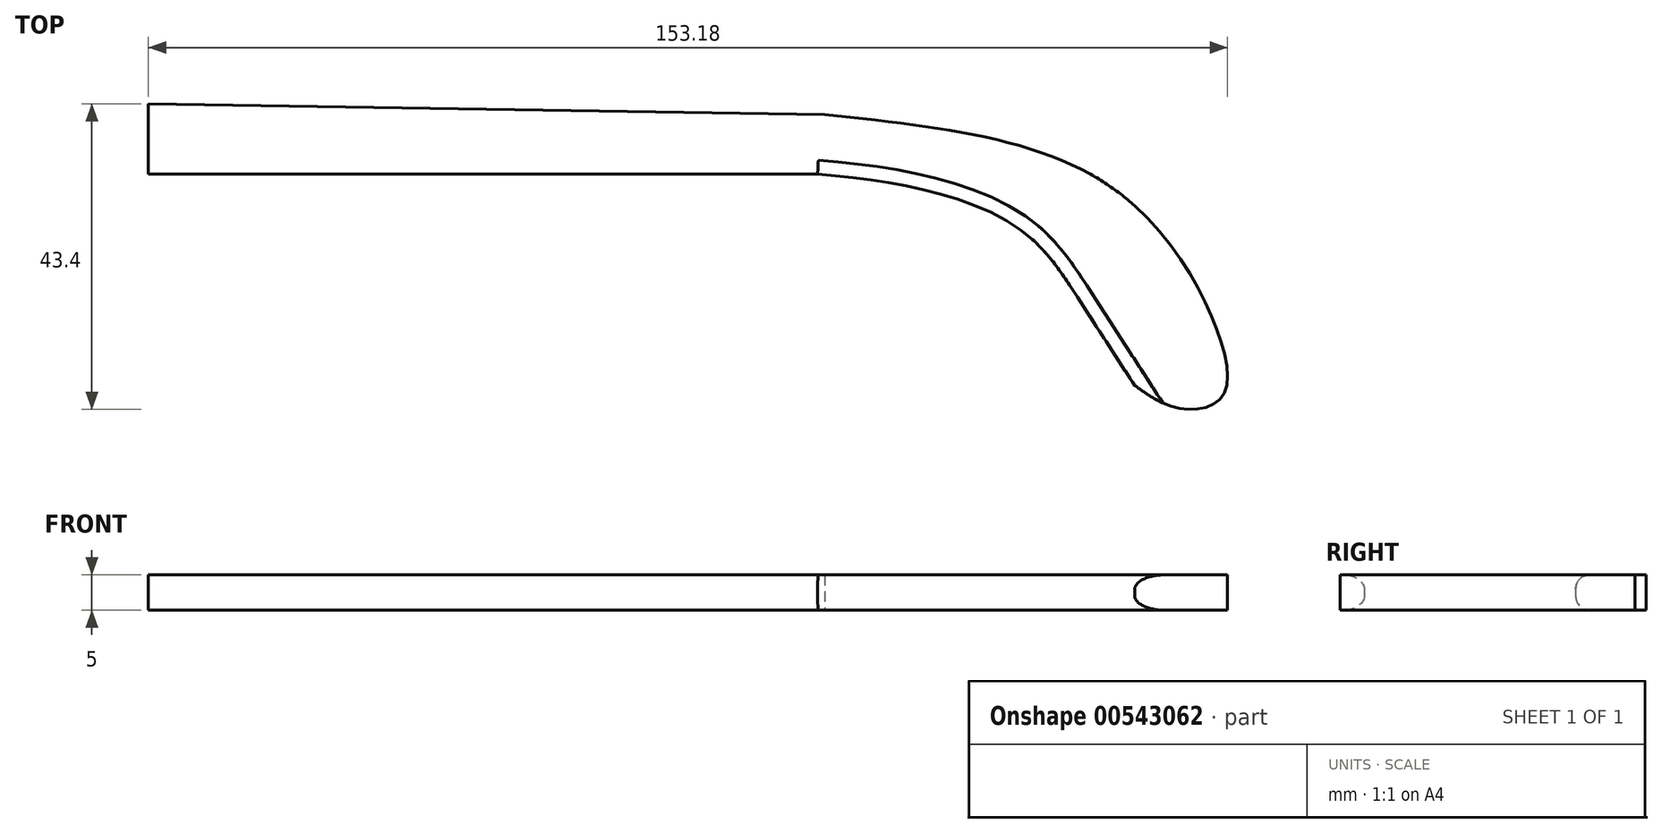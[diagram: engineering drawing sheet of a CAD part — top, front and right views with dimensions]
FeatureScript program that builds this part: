
annotation { "Feature Type Name" : "Feature", "Feature Type Description" : "" }
export const myFeature = defineFeature(function(context is Context, id is Id, definition is map)
    precondition{}
    {
        {
            var Q0;
            Q0=qCreatedBy(makeId("Top.planeOp"),FACE);
            var sketch = newSketch(context, id + "F0", { "sketchPlane" : qUnion([Q0])});
            skLineSegment(sketch, "E0", {"start": v(-30.6, 10) * mm, "end": v(-30.6, 0) * mm});
            skLineSegment(sketch, "E1", {"start": v(-30.6, 0) * mm, "end": v(27.4, 0) * mm});
            skLineSegment(sketch, "E2", {"start": v(27.4, 0) * mm, "end": v(64.4, 0) * mm});
            skLineSegment(sketch, "E3", {"start": v(65.4, 8.44) * mm, "end": v(-30.6, 10) * mm});
            skLineSegment(sketch, "E4", {"start": v(64.4, 0) * mm, "end": v(109.4, 0) * mm});
            skLineSegment(sketch, "E5", {"start": v(109.4, 0) * mm, "end": v(109.4, -30) * mm});
            skFitSpline(sketch, "E6", {"points": [v(64.4, 0) * mm, v(77.53, -1.77) * mm, v(93.12, -7.84) * mm, v(101.6, -17.95) * mm, v(109.4, -30) * mm], "startDerivative": vector(52.34, -4.8) * mm, "endDerivative": vector(31.66, -48.76) * mm});
            skFitSpline(sketch, "E7", {"points": [v(109.4, -30) * mm, v(115.71, -33.25) * mm, v(121.72, -31.72) * mm, v(120.95, -21.8) * mm, v(105.11, -1.2) * mm, v(65.4, 8.44) * mm], "startDerivative": vector(43.88, -31.29) * mm, "endDerivative": vector(-137.4, 14.26) * mm});
            skSolve(sketch);
        }
        {
            var Q0;
            Q0=makeQuery(id+"F0.imprint","IMPRINT",FACE,{"disambiguationData":[TD([[makeQuery(id+"F0.imprint","IMPRINT",EDGE,{"derivedFrom":sQuery(id+"F0.wireOp",EDGE,"E0")}),1.0]])]});
            var Q1;
            {var subQ0=sQuery(id+"F0.wireOp",EDGE,"E7");var subQ1=sQuery(id+"F0.wireOp",EDGE,"E5");var subQ3=makeQuery(id+"F0.imprint","INTERSECT",VERTEX,{"derivedFrom":[subQ1,subQ0]});Q1=makeQuery(id+"F0.imprint","IMPRINT",FACE,{"disambiguationData":[TD([[makeQuery(id+"F0.imprint","IMPRINT",EDGE,{"disambiguationData":[TD([[subQ3,-1.0]])],"derivedFrom":subQ1}),1.0]])]});}
            var Q2;
            {var subQ0=sQuery(id+"F0.wireOp",EDGE,"E6");Q2=makeQuery(id+"F0.imprint","IMPRINT",FACE,{"disambiguationData":[TD([[makeQuery(id+"F0.imprint","IMPRINT",EDGE,{"derivedFrom":subQ0}),1.0]])]});}
            extrude(context, id + "F1", {"entities" : qUnion([Q0, Q1, Q2]), "depth" : 5 * mm, "offsetDistance" : 25 * mm});
        }
        {
            var Q0;
            Q0=makeQuery(id+"F1.opExtrude","CAP_EDGE",EDGE,{"disambiguationData":[OSD([sQuery(id+"F0.wireOp",EDGE,"E6")])],"isStart":false});
            var Q1;
            Q1=makeQuery(id+"F1.opExtrude","CAP_EDGE",EDGE,{"disambiguationData":[OSD([sQuery(id+"F0.wireOp",EDGE,"E6")])],"isStart":true});
            fillet(context, id + "F2", {"entities" : qUnion([Q0, Q1]), "radius" : 2 * mm, "tangentPropagation" : true, "allowEdgeOverflow" : false});
        }
        {
            var Q0;
            Q0=makeQuery(id+"F1.opExtrude","CAP_EDGE",EDGE,{"disambiguationData":[OSD([sQuery(id+"F0.wireOp",EDGE,"E1"),sQuery(id+"F0.wireOp",EDGE,"E2")])],"isStart":false});
            var Q1;
            Q1=makeQuery(id+"F1.opExtrude","CAP_EDGE",EDGE,{"disambiguationData":[OSD([sQuery(id+"F0.wireOp",EDGE,"E1"),sQuery(id+"F0.wireOp",EDGE,"E2")])],"isStart":true});
            fillet(context, id + "F3", {"entities" : qUnion([Q0, Q1]), "radius" : 2 * mm, "tangentPropagation" : true, "allowEdgeOverflow" : false});
        }
    });
